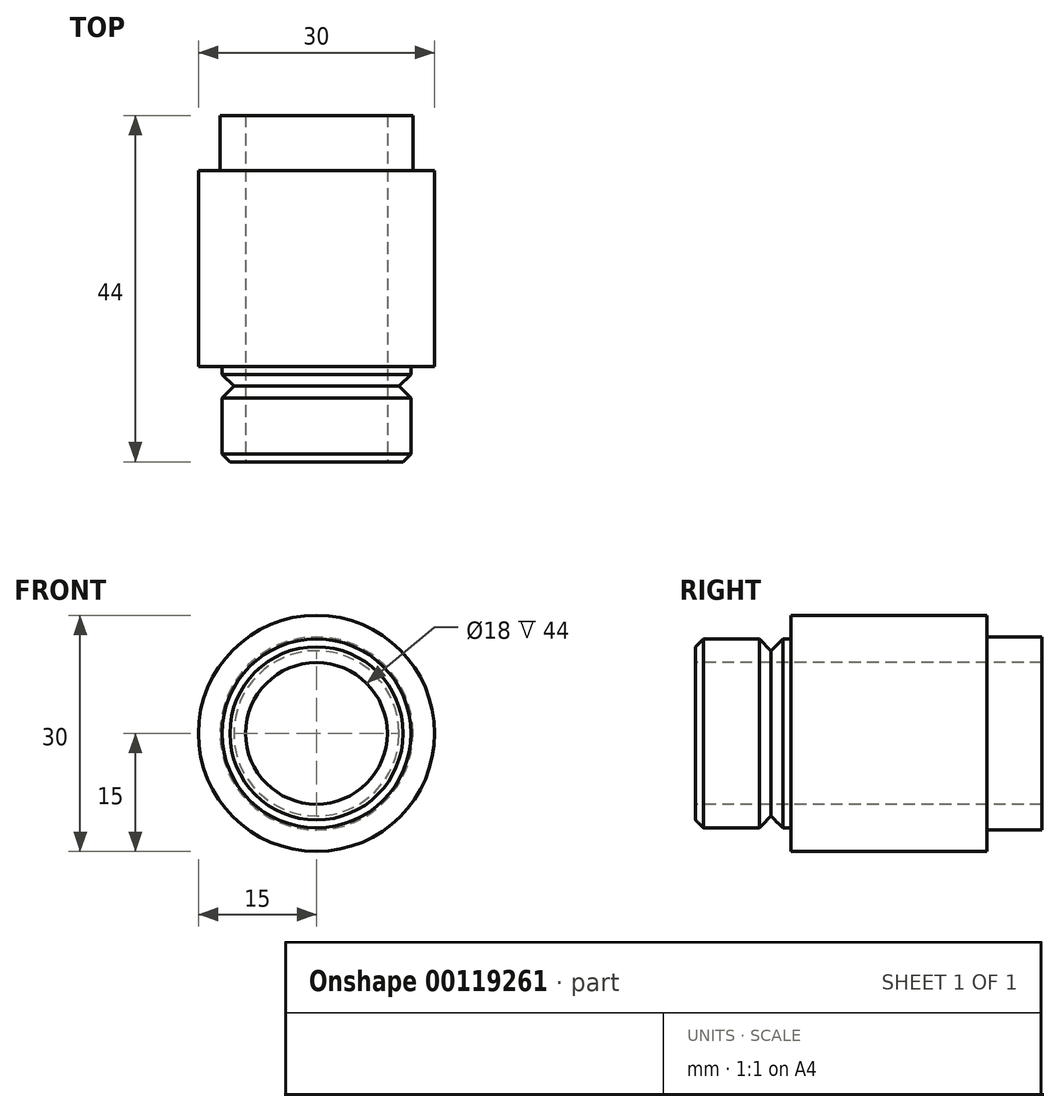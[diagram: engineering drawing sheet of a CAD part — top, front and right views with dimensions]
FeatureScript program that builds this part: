
annotation { "Feature Type Name" : "Feature", "Feature Type Description" : "" }
export const myFeature = defineFeature(function(context is Context, id is Id, definition is map)
    precondition{}
    {
        {
            var Q0;
            Q0=qCreatedBy(makeId("Right.planeOp"),FACE);
            var sketch = newSketch(context, id + "F0", { "sketchPlane" : qUnion([Q0])});
            skLineSegment(sketch, "E0", {"start": v(0, 0) * mm, "end": v(30.63, 0) * mm});
            skLineSegment(sketch, "E1", {"start": v(0, 9) * mm, "end": v(0, 12) * mm});
            skLineSegment(sketch, "E2", {"start": v(0, 12) * mm, "end": v(8.1, 12) * mm});
            skLineSegment(sketch, "E3", {"start": v(8.1, 12) * mm, "end": v(9.6, 10.5) * mm});
            skLineSegment(sketch, "E4", {"start": v(9.6, 10.5) * mm, "end": v(11.1, 12) * mm});
            skLineSegment(sketch, "E5", {"start": v(11.1, 12) * mm, "end": v(12.1, 12) * mm});
            skLineSegment(sketch, "E6", {"start": v(12.1, 12) * mm, "end": v(12.1, 15) * mm});
            skLineSegment(sketch, "E7", {"start": v(12.1, 15) * mm, "end": v(37, 15) * mm});
            skLineSegment(sketch, "E8", {"start": v(37, 15) * mm, "end": v(37, 12.25) * mm});
            skLineSegment(sketch, "E9", {"start": v(37, 12.25) * mm, "end": v(44, 12.25) * mm});
            skLineSegment(sketch, "E10", {"start": v(44, 12.25) * mm, "end": v(44, 9) * mm});
            skLineSegment(sketch, "E11", {"start": v(44, 9) * mm, "end": v(0, 9) * mm});
            skSolve(sketch);
        }
        {
            var Q0;
            Q0=makeQuery(id+"F0.imprint","IMPRINT",FACE,{"disambiguationData":[TD([[makeQuery(id+"F0.imprint","IMPRINT",EDGE,{"derivedFrom":sQuery(id+"F0.wireOp",EDGE,"E1")}),-1.0]])]});
            var Q1;
            Q1=sQuery(id+"F0.wireOp",EDGE,"E0");
            revolve(context, id + "F1", {"entities" : qUnion([Q0]), "axis" : qUnion([Q1]), "revolveType" : RevolveType.FULL});
        }
        {
            var Q0;
            Q0=makeQuery(id+"F1.opRevolve","SWEPT_EDGE",EDGE,{"disambiguationData":[OSD([sQuery(id+"F0.wireOp",EDGE,"E1"),sQuery(id+"F0.wireOp",EDGE,"E2")])]});
            chamfer(context, id + "F2", {"entities" : qUnion([Q0]), "width" : 1 * mm, "tangentPropagation" : true});
        }
    });
